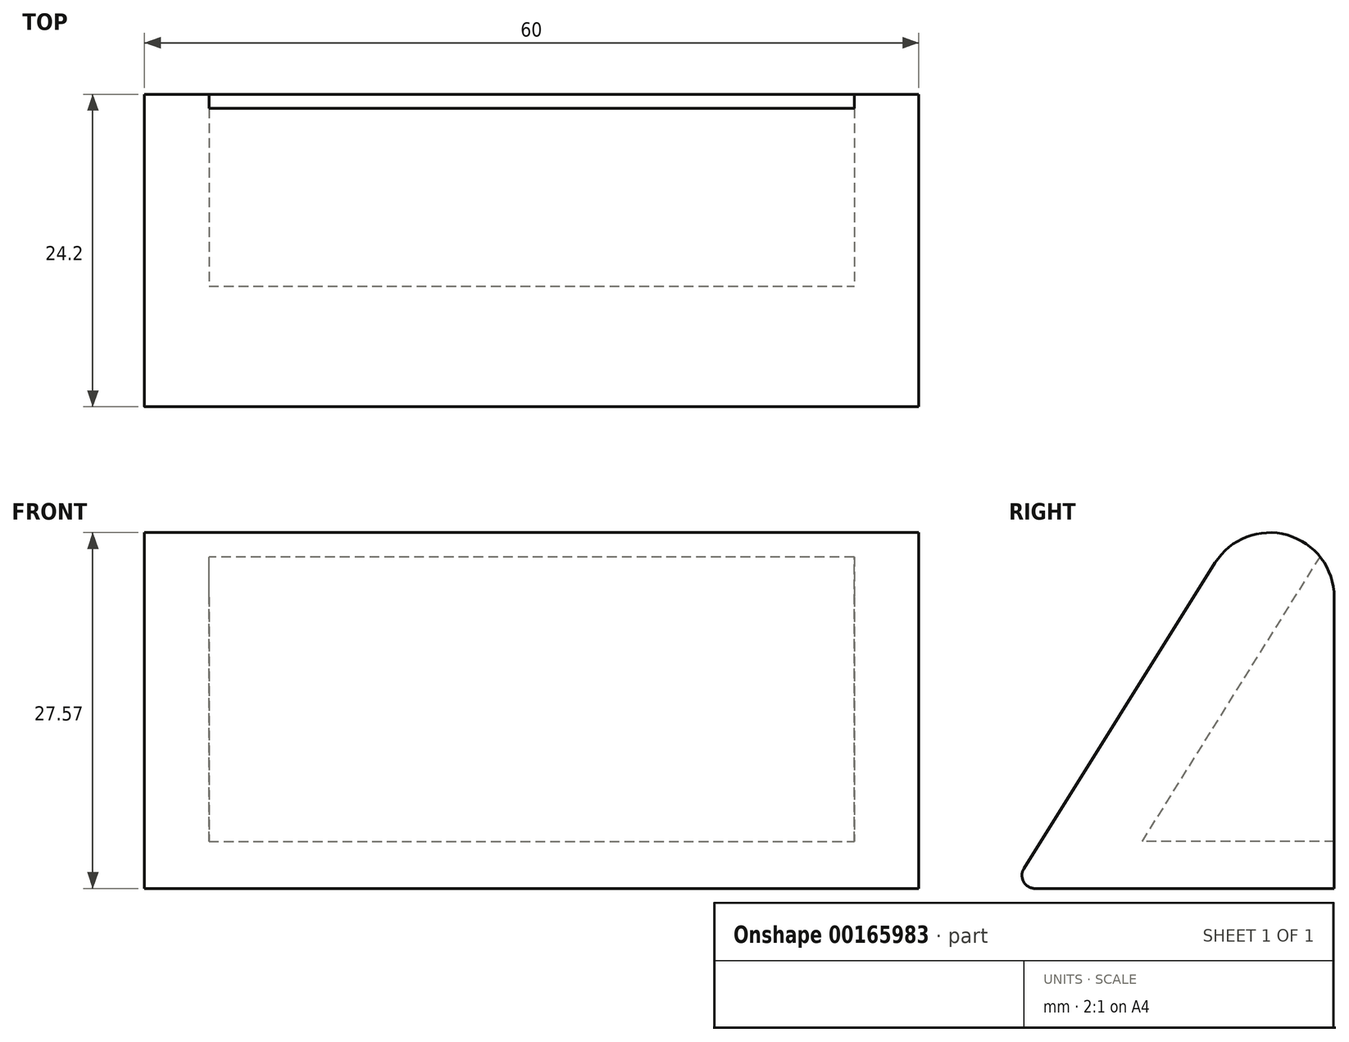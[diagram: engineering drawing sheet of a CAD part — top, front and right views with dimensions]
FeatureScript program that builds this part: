
annotation { "Feature Type Name" : "Feature", "Feature Type Description" : "" }
export const myFeature = defineFeature(function(context is Context, id is Id, definition is map)
    precondition{}
    {
        {
            var Q0;
            Q0=qCreatedBy(makeId("Right.planeOp"),FACE);
            var sketch = newSketch(context, id + "F0", { "sketchPlane" : qUnion([Q0])});
            skLineSegment(sketch, "E0", {"start": v(0, 0) * mm, "end": v(-25, 0) * mm});
            skLineSegment(sketch, "E1", {"start": v(-25, 0) * mm, "end": v(0, 40) * mm});
            skLineSegment(sketch, "E2", {"start": v(0, 40) * mm, "end": v(0, 0) * mm});
            skSolve(sketch);
        }
        {
            var Q0;
            Q0=makeQuery(id+"F0.imprint","IMPRINT",FACE,{"disambiguationData":[TD([[makeQuery(id+"F0.imprint","IMPRINT",EDGE,{"derivedFrom":sQuery(id+"F0.wireOp",EDGE,"E0")}),-1.0]])]});
            extrude(context, id + "F1", {"entities" : qUnion([Q0]), "depth" : 30 * mm});
        }
        {
            var Q0;
            Q0=makeQuery(id+"F1.opExtrude","CAP_FACE",FACE,{"disambiguationData":[OSD([sQuery(id+"F0.wireOp",EDGE,"E0"),sQuery(id+"F0.wireOp",EDGE,"E1"),sQuery(id+"F0.wireOp",EDGE,"E2")])],"isStart":false});
            var sketch = newSketch(context, id + "F2", { "sketchPlane" : qUnion([Q0])});
            skLineSegment(sketch, "E3", {"start": v(0, 3.64) * mm, "end": v(-14.88, 3.64) * mm});
            skLineSegment(sketch, "E4", {"start": v(-14.88, 3.64) * mm, "end": v(0, 27.44) * mm});
            skLineSegment(sketch, "E5", {"start": v(0, 27.44) * mm, "end": v(0, 3.64) * mm});
            skSolve(sketch);
        }
        {
            var Q0;
            Q0=makeQuery(id+"F2.imprint","IMPRINT",FACE,{"disambiguationData":[TD([[makeQuery(id+"F2.imprint","IMPRINT",EDGE,{"derivedFrom":sQuery(id+"F2.wireOp",EDGE,"E3")}),-1.0]])]});
            extrude(context, id + "F3", {"entities" : qUnion([Q0]), "operationType" : NewBodyOperationType.REMOVE, "oppositeDirection" : true, "depth" : 25 * mm});
        }
        {
            var Q0;
            Q0=makeQuery(id+"F1.opExtrude","SWEPT_BODY",BODY,{"disambiguationData":[OSD([sQuery(id+"F0.wireOp",EDGE,"E0"),sQuery(id+"F0.wireOp",EDGE,"E1"),sQuery(id+"F0.wireOp",EDGE,"E2")])]});
            var Q1;
            Q1=makeQuery(id+"F1.opExtrude","CAP_FACE",FACE,{"disambiguationData":[OSD([sQuery(id+"F0.wireOp",EDGE,"E0"),sQuery(id+"F0.wireOp",EDGE,"E1"),sQuery(id+"F0.wireOp",EDGE,"E2")])],"isStart":false});
            mirror(context, id + "F4", {"operationType" : NewBodyOperationType.ADD, "entities" : qUnion([Q0]), "mirrorPlane" : qUnion([Q1])});
        }
        {
            var Q0;
            {var subQ0=makeQuery(id+"F1.opExtrude","SWEPT_EDGE",EDGE,{"disambiguationData":[OSD([sQuery(id+"F0.wireOp",EDGE,"E1"),sQuery(id+"F0.wireOp",EDGE,"E2")])]});Q0=makeQuery(id+"F4.boolean.opBoolean","MERGE",EDGE,{"derivedFrom":[subQ0,makeQuery(id+"F4.opPattern","COPY",EDGE,{"derivedFrom":subQ0,"instanceName":"1"})]});}
            fillet(context, id + "F5", {"entities" : qUnion([Q0]), "radius" : 5 * mm, "tangentPropagation" : true, "allowEdgeOverflow" : false});
        }
        {
            var Q0;
            {var subQ0=makeQuery(id+"F1.opExtrude","SWEPT_EDGE",EDGE,{"disambiguationData":[OSD([sQuery(id+"F0.wireOp",EDGE,"E0"),sQuery(id+"F0.wireOp",EDGE,"E1")])]});Q0=makeQuery(id+"F4.boolean.opBoolean","MERGE",EDGE,{"derivedFrom":[subQ0,makeQuery(id+"F4.opPattern","COPY",EDGE,{"derivedFrom":subQ0,"instanceName":"1"})]});}
            fillet(context, id + "F6", {"entities" : qUnion([Q0]), "radius" : 1 * mm, "tangentPropagation" : true, "allowEdgeOverflow" : false});
        }
    });
